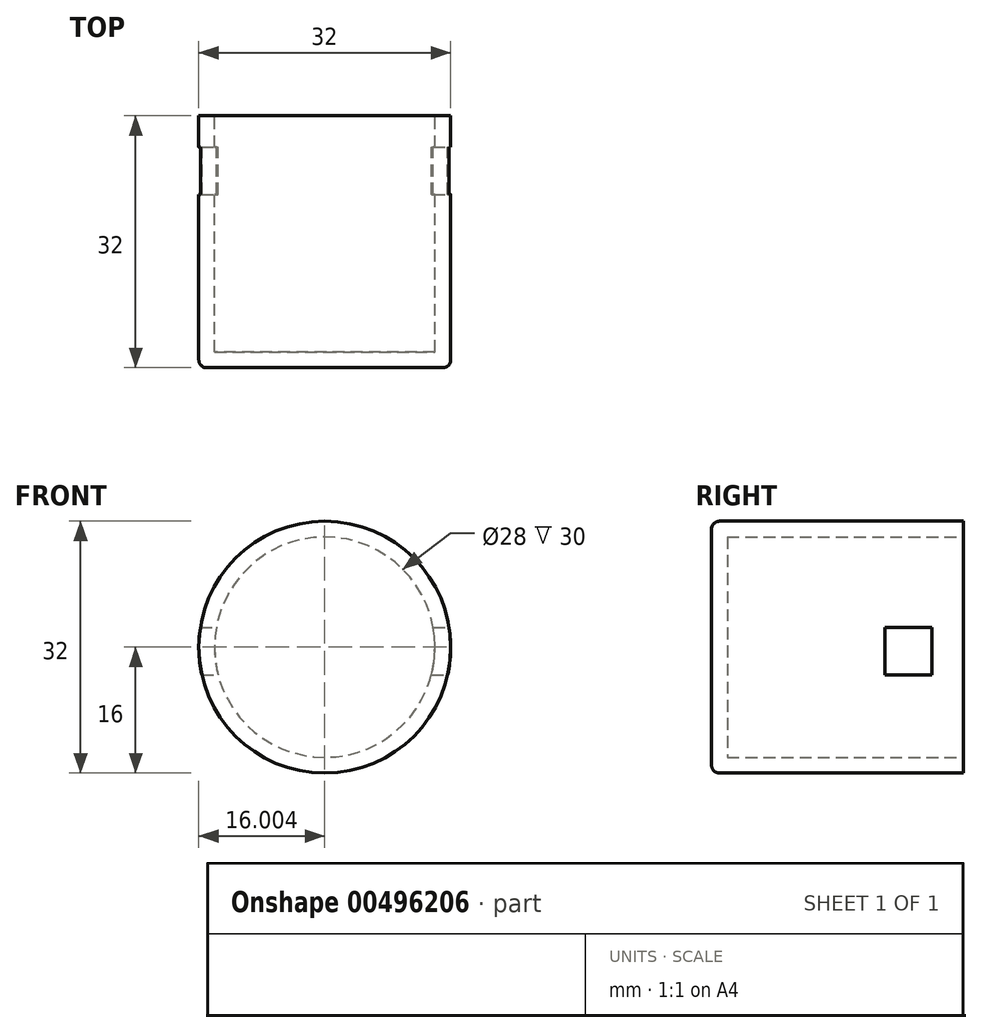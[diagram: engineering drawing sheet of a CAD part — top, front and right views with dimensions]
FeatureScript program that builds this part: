
annotation { "Feature Type Name" : "Feature", "Feature Type Description" : "" }
export const myFeature = defineFeature(function(context is Context, id is Id, definition is map)
    precondition{}
    {
        {
            var Q0;
            Q0=qCreatedBy(makeId("Front.planeOp"),FACE);
            var sketch = newSketch(context, id + "F0", { "sketchPlane" : qUnion([Q0])});
            skCircle(sketch, "E0", {"center": v(-13.57, 9.23) * mm, "radius": 16 * mm});
            skCircle(sketch, "E1", {"center": v(-13.57, 9.23) * mm, "radius": 14 * mm});
            skSolve(sketch);
        }
        {
            var Q0;
            Q0=makeQuery(id+"F0.imprint","IMPRINT",FACE,{"disambiguationData":[TD([[makeQuery(id+"F0.imprint","IMPRINT",EDGE,{"derivedFrom":sQuery(id+"F0.wireOp",EDGE,"E0")}),1.0]])]});
            var Q1;
            Q1=makeQuery(id+"F0.imprint","IMPRINT",FACE,{"disambiguationData":[TD([[makeQuery(id+"F0.imprint","IMPRINT",EDGE,{"derivedFrom":sQuery(id+"F0.wireOp",EDGE,"E1")}),1.0]])]});
            extrude(context, id + "F1", {"entities" : qUnion([Q0, Q1]), "depth" : 32 * mm});
        }
        {
            var Q0;
            Q0=makeQuery(id+"F1.opExtrude","CAP_FACE",FACE,{"disambiguationData":[OSD([sQuery(id+"F0.wireOp",EDGE,"E0")])],"isStart":true});
            var sketch = newSketch(context, id + "F2", { "sketchPlane" : qUnion([Q0])});
            skCircle(sketch, "E2", {"center": v(13.57, 9.23) * mm, "radius": 14 * mm});
            skSolve(sketch);
        }
        {
            var Q0;
            Q0 = qSketchRegion(id + "F1yOIOqaJ0OvniO_1", true);
            var Q1;
            Q1=makeQuery(id+"F2.imprint","IMPRINT",FACE,{"disambiguationData":[TD([[makeQuery(id+"F2.imprint","IMPRINT",EDGE,{"derivedFrom":sQuery(id+"F2.wireOp",EDGE,"E2")}),1.0]])]});
            var Q2;
            Q2 = qSketchRegion(id + "F5", true);
            extrude(context, id + "F3", {"entities" : qUnion([Q0, Q1, Q2]), "operationType" : NewBodyOperationType.REMOVE, "oppositeDirection" : true, "depth" : 30 * mm});
        }
        {
            var Q0;
            Q0=makeQuery(id+"F1.opExtrude","CAP_EDGE",EDGE,{"disambiguationData":[OSD([sQuery(id+"F0.wireOp",EDGE,"E0")])],"isStart":false});
            fillet(context, id + "F4", {"entities" : qUnion([Q0]), "radius" : 1 * mm, "tangentPropagation" : true, "allowEdgeOverflow" : false});
        }
        {
            var Q0;
            Q0=qCreatedBy(makeId("Right.planeOp"),FACE);
            var sketch = newSketch(context, id + "F5", { "sketchPlane" : qUnion([Q0])});
            skLineSegment(sketch, "E3.bottom", {"start": v(-10, 11.73) * mm, "end": v(-4, 11.73) * mm});
            skLineSegment(sketch, "E3.top", {"start": v(-10, 5.73) * mm, "end": v(-4, 5.73) * mm});
            skLineSegment(sketch, "E3.left", {"start": v(-10, 11.73) * mm, "end": v(-10, 5.73) * mm});
            skLineSegment(sketch, "E3.right", {"start": v(-4, 11.73) * mm, "end": v(-4, 5.73) * mm});
            skLineSegment(sketch, "E4", {"start": v(-4, 5.73) * mm, "end": v(-4, -9.27) * mm});
            skSolve(sketch);
        }
        {
            var Q0;
            Q0 = qSketchRegion(id + "F5", true);
            extrude(context, id + "F6", {"entities" : qUnion([Q0]), "operationType" : NewBodyOperationType.REMOVE, "oppositeDirection" : true, "depth" : 35.5 * mm, "hasSecondDirection" : true, "secondDirectionOppositeDirection" : false, "secondDirectionDepth" : 16.5 * mm});
        }
    });
